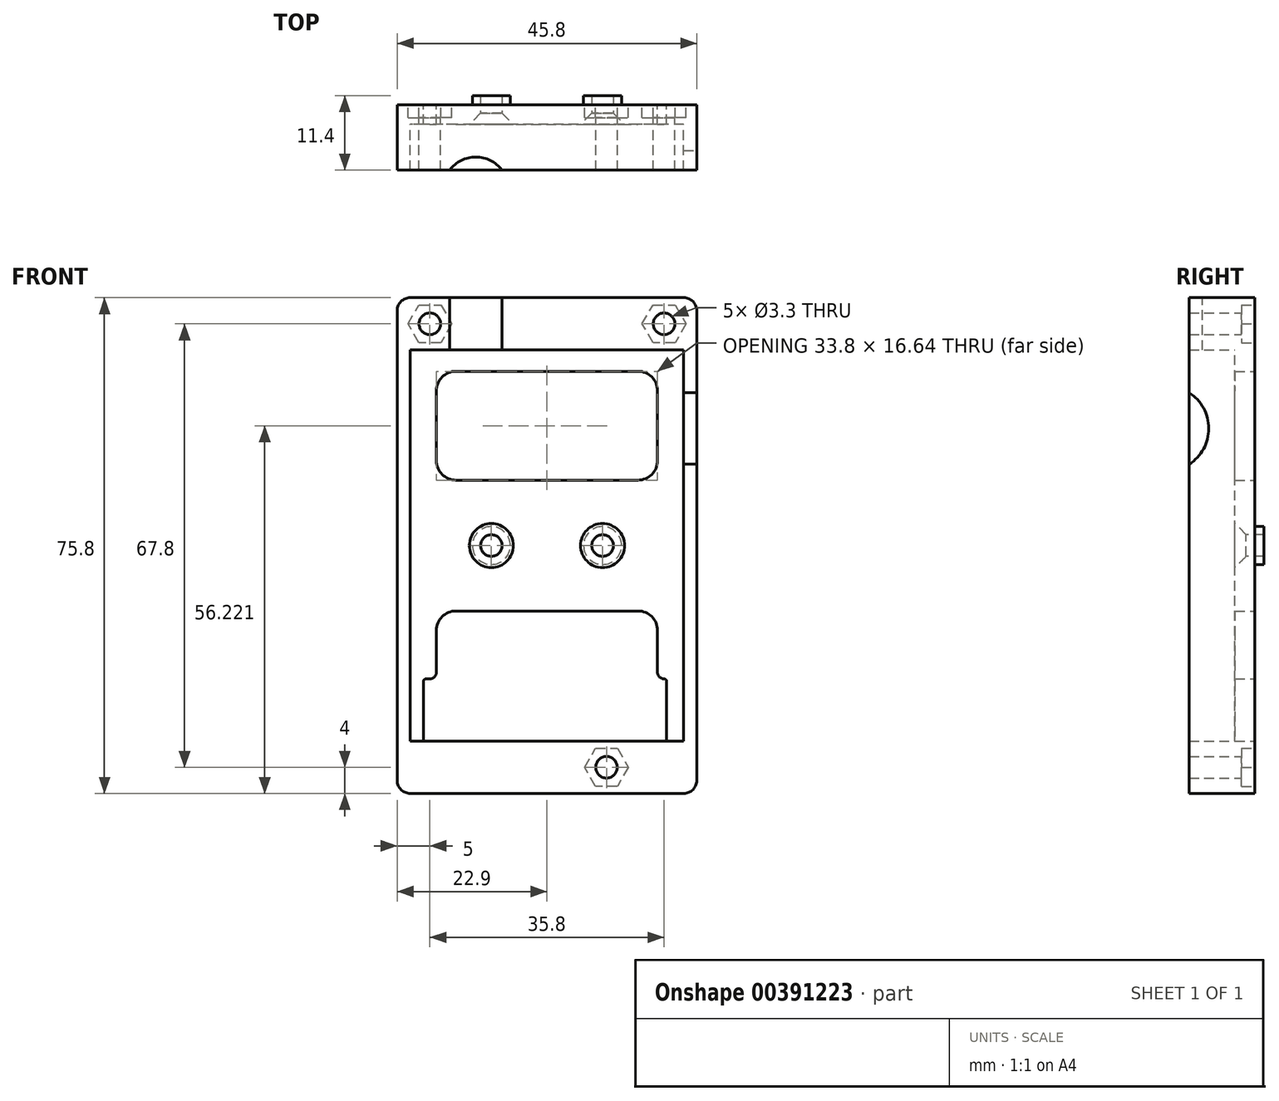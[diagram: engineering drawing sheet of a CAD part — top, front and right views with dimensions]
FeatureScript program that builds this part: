
annotation { "Feature Type Name" : "Feature", "Feature Type Description" : "" }
export const myFeature = defineFeature(function(context is Context, id is Id, definition is map)
    precondition{}
    {
        {
            var Q0;
            Q0=qCreatedBy(makeId("Front.planeOp"),FACE);
            var sketch = newSketch(context, id + "F0", { "sketchPlane" : qUnion([Q0])});
            skLineSegment(sketch, "E0.top", {"start": v(17.9, 37.9) * mm, "end": v(-17.9, 37.9) * mm});
            skPoint(sketch, "E0.middle", {"position": v(0, 0) * mm});
            skLineSegment(sketch, "E1.bottom", {"start": v(20.9, -29.9) * mm, "end": v(-20.9, -29.9) * mm});
            skLineSegment(sketch, "E1.top", {"start": v(20.9, 29.9) * mm, "end": v(-20.9, 29.9) * mm});
            skLineSegment(sketch, "E1.left", {"start": v(20.9, -29.9) * mm, "end": v(20.9, 29.9) * mm});
            skLineSegment(sketch, "E1.right", {"start": v(-20.9, -29.9) * mm, "end": v(-20.9, 29.9) * mm});
            skPoint(sketch, "E2", {"position": v(-16.9, 26.64) * mm});
            skPoint(sketch, "E3", {"position": v(16.9, 26.64) * mm});
            skPoint(sketch, "E4", {"position": v(18.3, -20.39) * mm});
            skPoint(sketch, "E5", {"position": v(-18.88, -20.39) * mm});
            skLineSegment(sketch, "E6", {"start": v(17.9, -20.39) * mm, "end": v(17.9, -20.39) * mm});
            skLineSegment(sketch, "E7", {"start": v(-17.9, -20.39) * mm, "end": v(-18.48, -20.39) * mm});
            skLineSegment(sketch, "E8", {"start": v(-18.88, -20.79) * mm, "end": v(-18.88, -29.9) * mm});
            skLineSegment(sketch, "E9", {"start": v(18.3, -29.9) * mm, "end": v(18.3, -20.79) * mm});
            skPoint(sketch, "E10", {"position": v(-16.9, -20.39) * mm});
            skPoint(sketch, "E11", {"position": v(16.9, -20.39) * mm});
            skLineSegment(sketch, "E12", {"start": v(-13.9, 26.64) * mm, "end": v(13.9, 26.64) * mm});
            skPoint(sketch, "E13", {"position": v(-8.5, 0) * mm});
            skPoint(sketch, "E14", {"position": v(8.5, 0) * mm});
            skCircle(sketch, "E15", {"center": v(-8.5, 0) * mm, "radius": 2.9 * mm});
            skCircle(sketch, "E16", {"center": v(8.5, 0) * mm, "radius": 2.9 * mm});
            skPoint(sketch, "E17.visualSharp", {"position": v(-22.9, 37.9) * mm});
            skPoint(sketch, "E18.visualSharp", {"position": v(22.9, 37.9) * mm});
            skPoint(sketch, "E19.visualSharp", {"position": v(22.9, -37.9) * mm});
            skPoint(sketch, "E20.visualSharp", {"position": v(-22.9, -37.9) * mm});
            skArc(sketch, "E21.filletArc", {"start": v(-13.9, 26.64) * mm, "mid": v(-16.02, 25.76) * mm, "end": v(-16.9, 23.64) * mm});
            skArc(sketch, "E22.filletArc", {"start": v(16.9, 23.64) * mm, "mid": v(16.02, 25.76) * mm, "end": v(13.9, 26.64) * mm});
            skArc(sketch, "E23.filletArc", {"start": v(16.9, -19.39) * mm, "mid": v(17.2, -20.1) * mm, "end": v(17.9, -20.39) * mm});
            skArc(sketch, "E24.filletArc", {"start": v(18.3, -20.79) * mm, "mid": v(18.18, -20.5) * mm, "end": v(17.9, -20.39) * mm});
            skArc(sketch, "E25.filletArc", {"start": v(-17.9, -20.39) * mm, "mid": v(-17.2, -20.1) * mm, "end": v(-16.9, -19.39) * mm});
            skArc(sketch, "E26.filletArc", {"start": v(-18.48, -20.39) * mm, "mid": v(-18.76, -20.5) * mm, "end": v(-18.88, -20.79) * mm});
            skLineSegment(sketch, "E27", {"start": v(-22.9, 32.9) * mm, "end": v(-22.9, -35.9) * mm});
            skLineSegment(sketch, "E28", {"start": v(20.9, -37.9) * mm, "end": v(-20.9, -37.9) * mm});
            skLineSegment(sketch, "E29", {"start": v(22.9, -35.9) * mm, "end": v(22.9, 32.9) * mm});
            skPoint(sketch, "E30", {"position": v(-10.9, 37.9) * mm});
            skPoint(sketch, "E31", {"position": v(-17.9, 32.9) * mm});
            skPoint(sketch, "E32", {"position": v(17.9, 32.9) * mm});
            skPoint(sketch, "E33", {"position": v(9.1, -33.9) * mm});
            skPoint(sketch, "E34", {"position": v(-17.9, 33.9) * mm});
            skPoint(sketch, "E35", {"position": v(17.9, 33.9) * mm});
            skCircle(sketch, "E36.cCircle", {"center": v(-17.9, 33.9) * mm, "radius": 2.9 * mm, "construction": true});
            skLineSegment(sketch, "E36.0", {"start": v(-14.55, 33.9) * mm, "end": v(-16.23, 31) * mm});
            skLineSegment(sketch, "E36.1", {"start": v(-16.23, 31) * mm, "end": v(-19.57, 31) * mm});
            skLineSegment(sketch, "E36.2", {"start": v(-19.57, 31) * mm, "end": v(-21.25, 33.9) * mm});
            skLineSegment(sketch, "E36.3", {"start": v(-21.25, 33.9) * mm, "end": v(-19.57, 36.8) * mm});
            skLineSegment(sketch, "E36.4", {"start": v(-19.57, 36.8) * mm, "end": v(-16.23, 36.8) * mm});
            skLineSegment(sketch, "E36.5", {"start": v(-16.23, 36.8) * mm, "end": v(-14.55, 33.9) * mm});
            skPoint(sketch, "E36.0.midPoint", {"position": v(-15.39, 32.45) * mm});
            skCircle(sketch, "E37.cCircle", {"center": v(17.9, 33.9) * mm, "radius": 2.9 * mm, "construction": true});
            skLineSegment(sketch, "E37.0", {"start": v(19.57, 31) * mm, "end": v(16.23, 31) * mm});
            skLineSegment(sketch, "E37.1", {"start": v(16.23, 31) * mm, "end": v(14.55, 33.9) * mm});
            skLineSegment(sketch, "E37.2", {"start": v(14.55, 33.9) * mm, "end": v(16.23, 36.8) * mm});
            skLineSegment(sketch, "E37.3", {"start": v(16.23, 36.8) * mm, "end": v(19.57, 36.8) * mm});
            skLineSegment(sketch, "E37.4", {"start": v(19.57, 36.8) * mm, "end": v(21.25, 33.9) * mm});
            skLineSegment(sketch, "E37.5", {"start": v(21.25, 33.9) * mm, "end": v(19.57, 31) * mm});
            skPoint(sketch, "E37.0.midPoint", {"position": v(17.9, 31) * mm});
            skCircle(sketch, "E38.cCircle", {"center": v(9.1, -33.9) * mm, "radius": 2.9 * mm, "construction": true});
            skLineSegment(sketch, "E38.0", {"start": v(10.77, -31) * mm, "end": v(12.45, -33.9) * mm});
            skLineSegment(sketch, "E38.1", {"start": v(12.45, -33.9) * mm, "end": v(10.77, -36.8) * mm});
            skLineSegment(sketch, "E38.2", {"start": v(10.77, -36.8) * mm, "end": v(7.43, -36.8) * mm});
            skLineSegment(sketch, "E38.3", {"start": v(7.43, -36.8) * mm, "end": v(5.75, -33.9) * mm});
            skLineSegment(sketch, "E38.4", {"start": v(5.75, -33.9) * mm, "end": v(7.43, -31) * mm});
            skLineSegment(sketch, "E38.5", {"start": v(7.43, -31) * mm, "end": v(10.77, -31) * mm});
            skPoint(sketch, "E38.0.midPoint", {"position": v(11.61, -32.45) * mm});
            skLineSegment(sketch, "E39", {"start": v(22.9, 35.9) * mm, "end": v(22.9, 32.9) * mm});
            skLineSegment(sketch, "E40", {"start": v(17.9, 37.9) * mm, "end": v(20.9, 37.9) * mm});
            skLineSegment(sketch, "E41", {"start": v(-17.9, 37.9) * mm, "end": v(-20.9, 37.9) * mm});
            skLineSegment(sketch, "E42", {"start": v(-22.9, 35.9) * mm, "end": v(-22.9, 32.9) * mm});
            skArc(sketch, "E43.filletArc", {"start": v(-20.9, 37.9) * mm, "mid": v(-22.31, 37.31) * mm, "end": v(-22.9, 35.9) * mm});
            skArc(sketch, "E44.filletArc", {"start": v(22.9, 35.9) * mm, "mid": v(22.31, 37.31) * mm, "end": v(20.9, 37.9) * mm});
            skArc(sketch, "E45.filletArc", {"start": v(20.9, -37.9) * mm, "mid": v(22.31, -37.31) * mm, "end": v(22.9, -35.9) * mm});
            skArc(sketch, "E46.filletArc", {"start": v(-22.9, -35.9) * mm, "mid": v(-22.31, -37.31) * mm, "end": v(-20.9, -37.9) * mm});
            skLineSegment(sketch, "E47", {"start": v(-13.9, 10) * mm, "end": v(13.9, 10) * mm});
            skLineSegment(sketch, "E48", {"start": v(-16.9, 13) * mm, "end": v(-16.9, 23.64) * mm});
            skLineSegment(sketch, "E49", {"start": v(16.9, 13) * mm, "end": v(16.9, 23.64) * mm});
            skPoint(sketch, "E50.visualSharp", {"position": v(-16.9, 10) * mm});
            skArc(sketch, "E50.filletArc", {"start": v(-16.9, 13) * mm, "mid": v(-16.02, 10.88) * mm, "end": v(-13.9, 10) * mm});
            skPoint(sketch, "E51.visualSharp", {"position": v(16.9, 10) * mm});
            skArc(sketch, "E51.filletArc", {"start": v(13.9, 10) * mm, "mid": v(16.02, 10.88) * mm, "end": v(16.9, 13) * mm});
            skLineSegment(sketch, "E52", {"start": v(-13.9, -10) * mm, "end": v(13.9, -10) * mm});
            skLineSegment(sketch, "E53", {"start": v(16.9, -19.39) * mm, "end": v(16.9, -13) * mm});
            skLineSegment(sketch, "E54", {"start": v(-16.9, -13) * mm, "end": v(-16.9, -19.39) * mm});
            skPoint(sketch, "E55.visualSharp", {"position": v(-16.9, -10) * mm});
            skArc(sketch, "E55.filletArc", {"start": v(-13.9, -10) * mm, "mid": v(-16.02, -10.88) * mm, "end": v(-16.9, -13) * mm});
            skPoint(sketch, "E56.visualSharp", {"position": v(16.9, -10) * mm});
            skArc(sketch, "E56.filletArc", {"start": v(16.9, -13) * mm, "mid": v(16.02, -10.88) * mm, "end": v(13.9, -10) * mm});
            skSolve(sketch);
        }
        {
            var Q0;
            Q0=makeQuery(id+"F0.imprint","IMPRINT",FACE,{"disambiguationData":[TD([[makeQuery(id+"F0.imprint","IMPRINT",EDGE,{"derivedFrom":sQuery(id+"F0.wireOp",EDGE,"E0.top")}),1.0]])]});
            var Q1;
            Q1=makeQuery(id+"F0.imprint","IMPRINT",FACE,{"disambiguationData":[TD([[makeQuery(id+"F0.imprint","IMPRINT",EDGE,{"derivedFrom":sQuery(id+"F0.wireOp",EDGE,"E36.0")}),-1.0]])]});
            var Q2;
            Q2=makeQuery(id+"F0.imprint","IMPRINT",FACE,{"disambiguationData":[TD([[makeQuery(id+"F0.imprint","IMPRINT",EDGE,{"derivedFrom":sQuery(id+"F0.wireOp",EDGE,"E37.0")}),-1.0]])]});
            var Q3;
            Q3=makeQuery(id+"F0.imprint","IMPRINT",FACE,{"disambiguationData":[TD([[makeQuery(id+"F0.imprint","IMPRINT",EDGE,{"derivedFrom":sQuery(id+"F0.wireOp",EDGE,"E38.0")}),-1.0]])]});
            extrude(context, id + "F1", {"entities" : qUnion([Q0, Q1, Q2, Q3]), "depth" : 10 * mm});
        }
        {
            var Q0;
            Q0=makeQuery(id+"F0.imprint","IMPRINT",FACE,{"disambiguationData":[TD([[makeQuery(id+"F0.imprint","IMPRINT",EDGE,{"derivedFrom":sQuery(id+"F0.wireOp",EDGE,"E1.top")}),1.0]])]});
            var Q1;
            Q1=makeQuery(id+"F0.imprint","IMPRINT",FACE,{"disambiguationData":[TD([[makeQuery(id+"F0.imprint","IMPRINT",EDGE,{"derivedFrom":sQuery(id+"F0.wireOp",EDGE,"E15")}),1.0]])]});
            var Q2;
            Q2=makeQuery(id+"F0.imprint","IMPRINT",FACE,{"disambiguationData":[TD([[makeQuery(id+"F0.imprint","IMPRINT",EDGE,{"derivedFrom":sQuery(id+"F0.wireOp",EDGE,"E16")}),1.0]])]});
            extrude(context, id + "F2", {"entities" : qUnion([Q0, Q1, Q2]), "operationType" : NewBodyOperationType.ADD, "depth" : 3 * mm});
        }
        {
            var Q0;
            Q0=makeQuery(id+"F1.opExtrude","SWEPT_FACE",FACE,{"disambiguationData":[OSD([sQuery(id+"F0.wireOp",EDGE,"E29")])]});
            var sketch = newSketch(context, id + "F3", { "sketchPlane" : qUnion([Q0])});
            skPoint(sketch, "E57", {"position": v(-5, 17.9) * mm});
            skPoint(sketch, "E58", {"position": v(-13.5, 17.9) * mm});
            skCircle(sketch, "E59", {"center": v(-13.5, 17.9) * mm, "radius": 6.5 * mm});
            skSolve(sketch);
        }
        {
            var Q0;
            Q0=qSketchRegion(id+"F3",true);
            extrude(context, id + "F4", {"entities" : qUnion([Q0]), "operationType" : NewBodyOperationType.REMOVE, "oppositeDirection" : true, "depth" : 4 * mm});
        }
        {
            var Q0;
            Q0=makeQuery(id+"F1.opExtrude","SWEPT_FACE",FACE,{"disambiguationData":[OSD([sQuery(id+"F0.wireOp",EDGE,"E0.top")])]});
            var sketch = newSketch(context, id + "F5", { "sketchPlane" : qUnion([Q0])});
            skPoint(sketch, "E60", {"position": v(-10.87, 0) * mm});
            skPoint(sketch, "E61", {"position": v(-10.87, -13) * mm});
            skCircle(sketch, "E62", {"center": v(-10.87, -13) * mm, "radius": 5 * mm});
            skSolve(sketch);
        }
        {
            var Q0;
            Q0=qSketchRegion(id+"F5",true);
            extrude(context, id + "F6", {"entities" : qUnion([Q0]), "operationType" : NewBodyOperationType.REMOVE, "oppositeDirection" : true, "depth" : 12 * mm});
        }
        {
            var Q0;
            Q0=makeQuery(id+"F0.imprint","IMPRINT",FACE,{"disambiguationData":[TD([[makeQuery(id+"F0.imprint","IMPRINT",EDGE,{"derivedFrom":sQuery(id+"F0.wireOp",EDGE,"E36.0")}),-1.0]])]});
            var Q1;
            Q1=makeQuery(id+"F0.imprint","IMPRINT",FACE,{"disambiguationData":[TD([[makeQuery(id+"F0.imprint","IMPRINT",EDGE,{"derivedFrom":sQuery(id+"F0.wireOp",EDGE,"E37.0")}),-1.0]])]});
            var Q2;
            Q2=makeQuery(id+"F0.imprint","IMPRINT",FACE,{"disambiguationData":[TD([[makeQuery(id+"F0.imprint","IMPRINT",EDGE,{"derivedFrom":sQuery(id+"F0.wireOp",EDGE,"E38.0")}),-1.0]])]});
            extrude(context, id + "F7", {"entities" : qUnion([Q0, Q1, Q2]), "operationType" : NewBodyOperationType.REMOVE, "depth" : 2 * mm});
        }
        {
            var Q0;
            Q0=sQuery(id+"F0.wireOp",VERTEX,"E34");
            var Q1;
            Q1=sQuery(id+"F0.wireOp",VERTEX,"E35");
            var Q2;
            Q2=sQuery(id+"F0.wireOp",VERTEX,"E33");
            var Q3;
            Q3=makeQuery(id+"F1.opExtrude","SWEPT_BODY",BODY,{"disambiguationData":[OSD([sQuery(id+"F0.wireOp",EDGE,"E0.top"),sQuery(id+"F0.wireOp",EDGE,"E1.bottom"),sQuery(id+"F0.wireOp",EDGE,"E1.top"),sQuery(id+"F0.wireOp",EDGE,"E1.left"),sQuery(id+"F0.wireOp",EDGE,"E1.right"),sQuery(id+"F0.wireOp",EDGE,"E17.filletArc"),sQuery(id+"F0.wireOp",EDGE,"E18.filletArc"),sQuery(id+"F0.wireOp",EDGE,"E27"),sQuery(id+"F0.wireOp",EDGE,"E28"),sQuery(id+"F0.wireOp",EDGE,"E29")])]});
            hole(context, id + "F8", {"style" : HoleStyle.SIMPLE, "endStyle" : HoleEndStyle.BLIND, "oppositeDirection" : true, "standardTappedOrClearance" : lookupTablePath({ "standard" : "ISO", "fit" : "Normal", "size" : "M3", "type" : "Clearance" }), "standardBlindInLast" : lookupTablePath({ "fit" : "Standard", "standard" : "ISO", "size" : "M3", "type" : "Clearance" }), "holeDiameter" : 3.3 * mm, "holeDepth" : 13.8 * mm, "tappedDepth" : 12 * mm, "tapClearance" : 3, "locations" : qUnion([Q0, Q1, Q2]), "scope" : qUnion([Q3])});
        }
        {
            var Q0;
            Q0=makeQuery(id+"F0.imprint","IMPRINT",FACE,{"disambiguationData":[TD([[makeQuery(id+"F0.imprint","IMPRINT",EDGE,{"derivedFrom":sQuery(id+"F0.wireOp",EDGE,"E16")}),1.0]])]});
            var Q1;
            Q1=makeQuery(id+"F0.imprint","IMPRINT",FACE,{"disambiguationData":[TD([[makeQuery(id+"F0.imprint","IMPRINT",EDGE,{"derivedFrom":sQuery(id+"F0.wireOp",EDGE,"E15")}),1.0]])]});
            extrude(context, id + "F9", {"entities" : qUnion([Q0, Q1]), "operationType" : NewBodyOperationType.ADD, "oppositeDirection" : true, "depth" : 1.4 * mm});
        }
        {
            var Q0;
            Q0=sQuery(id+"F0.wireOp",VERTEX,"E13");
            var Q1;
            Q1=sQuery(id+"F0.wireOp",VERTEX,"E14");
            var Q2;
            Q2=makeQuery(id+"F1.opExtrude","SWEPT_BODY",BODY,{"disambiguationData":[OSD([sQuery(id+"F0.wireOp",EDGE,"E0.top"),sQuery(id+"F0.wireOp",EDGE,"E1.bottom"),sQuery(id+"F0.wireOp",EDGE,"E1.top"),sQuery(id+"F0.wireOp",EDGE,"E1.left"),sQuery(id+"F0.wireOp",EDGE,"E1.right"),sQuery(id+"F0.wireOp",EDGE,"E27"),sQuery(id+"F0.wireOp",EDGE,"E28"),sQuery(id+"F0.wireOp",EDGE,"E29"),sQuery(id+"F0.wireOp",EDGE,"E39"),sQuery(id+"F0.wireOp",EDGE,"E40"),sQuery(id+"F0.wireOp",EDGE,"E41"),sQuery(id+"F0.wireOp",EDGE,"E42"),sQuery(id+"F0.wireOp",EDGE,"E43.filletArc"),sQuery(id+"F0.wireOp",EDGE,"E44.filletArc"),sQuery(id+"F0.wireOp",EDGE,"E45.filletArc"),sQuery(id+"F0.wireOp",EDGE,"E46.filletArc")])]});
            hole(context, id + "F10", {"style" : HoleStyle.SIMPLE, "endStyle" : HoleEndStyle.BLIND, "standardTappedOrClearance" : lookupTablePath({ "standard" : "ISO", "fit" : "Normal", "size" : "M3", "type" : "Clearance" }), "standardBlindInLast" : lookupTablePath({ "fit" : "Standard", "standard" : "ISO", "size" : "M3", "type" : "Clearance" }), "holeDiameter" : 3.3 * mm, "holeDepth" : 8 * mm, "tappedDepth" : 12 * mm, "tapClearance" : 3, "locations" : qUnion([Q0, Q1]), "scope" : qUnion([Q2])});
        }
        {
            var Q0;
            Q0=makeQuery(id+"F2.opExtrude","CAP_FACE",FACE,{"disambiguationData":[OSD([sQuery(id+"F0.wireOp",EDGE,"E1.bottom"),sQuery(id+"F0.wireOp",EDGE,"E1.top"),sQuery(id+"F0.wireOp",EDGE,"E1.left"),sQuery(id+"F0.wireOp",EDGE,"E1.right"),sQuery(id+"F0.wireOp",EDGE,"E7"),sQuery(id+"F0.wireOp",EDGE,"E8"),sQuery(id+"F0.wireOp",EDGE,"E9"),sQuery(id+"F0.wireOp",EDGE,"E12"),sQuery(id+"F0.wireOp",EDGE,"K6XqkS5L-WGHN-TWgH-c4nJ-z8t4pHJzCrDJ"),sQuery(id+"F0.wireOp",EDGE,"AOEySlmF-0j6P-qqkT-EpBq-kiaK5CICxXme"),sQuery(id+"F0.wireOp",EDGE,"E21.filletArc"),sQuery(id+"F0.wireOp",EDGE,"E22.filletArc"),sQuery(id+"F0.wireOp",EDGE,"E23.filletArc"),sQuery(id+"F0.wireOp",EDGE,"E24.filletArc"),sQuery(id+"F0.wireOp",EDGE,"E25.filletArc"),sQuery(id+"F0.wireOp",EDGE,"E26.filletArc"),sQuery(id+"F0.wireOp",EDGE,"DrI3f7R3-oS3S-RcJZ-1jdH-4EDYyidPOq7r"),sQuery(id+"F0.wireOp",EDGE,"3SI2AoPm-MffP-7Fup-86XO-qDeTtpTrlcJ3"),sQuery(id+"F0.wireOp",EDGE,"LnKR15x0-CBta-H6yr-Udcb-2uIxGwJZttCQ"),sQuery(id+"F0.wireOp",EDGE,"2DFLZ99V-HUzz-hA2j-pxHP-NyHY5f3DKzBv"),sQuery(id+"F0.wireOp",EDGE,"6e5e6a54-4a18-4804-a338-8922faaae2a8.filletArc"),sQuery(id+"F0.wireOp",EDGE,"3de4d2fc-e988-40a3-922c-9fbc6863065a.filletArc"),sQuery(id+"F0.wireOp",EDGE,"8a437a8d-4504-4dbb-8b88-49b5f11e028d.filletArc"),sQuery(id+"F0.wireOp",EDGE,"d99b9da6-05cb-415f-a28c-bb240d361167.filletArc")])],"isStart":false});
            var sketch = newSketch(context, id + "F11", { "sketchPlane" : qUnion([Q0])});
            skPoint(sketch, "E63", {"position": v(8.5, 0) * mm});
            skPoint(sketch, "E64", {"position": v(-8.5, 0) * mm});
            skSolve(sketch);
        }
        {
            var Q0;
            Q0=sQuery(id+"F11.wireOp",VERTEX,"E64");
            var Q1;
            Q1=sQuery(id+"F11.wireOp",VERTEX,"E63");
            var Q2;
            Q2=makeQuery(id+"F1.opExtrude","SWEPT_BODY",BODY,{"disambiguationData":[OSD([sQuery(id+"F0.wireOp",EDGE,"E0.top"),sQuery(id+"F0.wireOp",EDGE,"E1.bottom"),sQuery(id+"F0.wireOp",EDGE,"E1.top"),sQuery(id+"F0.wireOp",EDGE,"E1.left"),sQuery(id+"F0.wireOp",EDGE,"E1.right"),sQuery(id+"F0.wireOp",EDGE,"E27"),sQuery(id+"F0.wireOp",EDGE,"E28"),sQuery(id+"F0.wireOp",EDGE,"E29"),sQuery(id+"F0.wireOp",EDGE,"E39"),sQuery(id+"F0.wireOp",EDGE,"E40"),sQuery(id+"F0.wireOp",EDGE,"E41"),sQuery(id+"F0.wireOp",EDGE,"E42"),sQuery(id+"F0.wireOp",EDGE,"E43.filletArc"),sQuery(id+"F0.wireOp",EDGE,"E44.filletArc"),sQuery(id+"F0.wireOp",EDGE,"E45.filletArc"),sQuery(id+"F0.wireOp",EDGE,"E46.filletArc")])]});
            hole(context, id + "F12", {"style" : HoleStyle.C_SINK, "endStyle" : HoleEndStyle.BLIND, "standardTappedOrClearance" : lookupTablePath({ "standard" : "ISO", "fit" : "Normal", "size" : "M3", "type" : "Clearance" }), "standardBlindInLast" : lookupTablePath({ "fit" : "Standard", "standard" : "ISO", "size" : "M3", "type" : "Clearance" }), "holeDiameter" : 3.3 * mm, "cSinkDiameter" : 6.72 * mm, "cSinkAngle" : 90 * degree, "holeDepth" : 8 * mm, "tappedDepth" : 12 * mm, "tapClearance" : 3, "locations" : qUnion([Q0, Q1]), "scope" : qUnion([Q2])});
        }
    });
